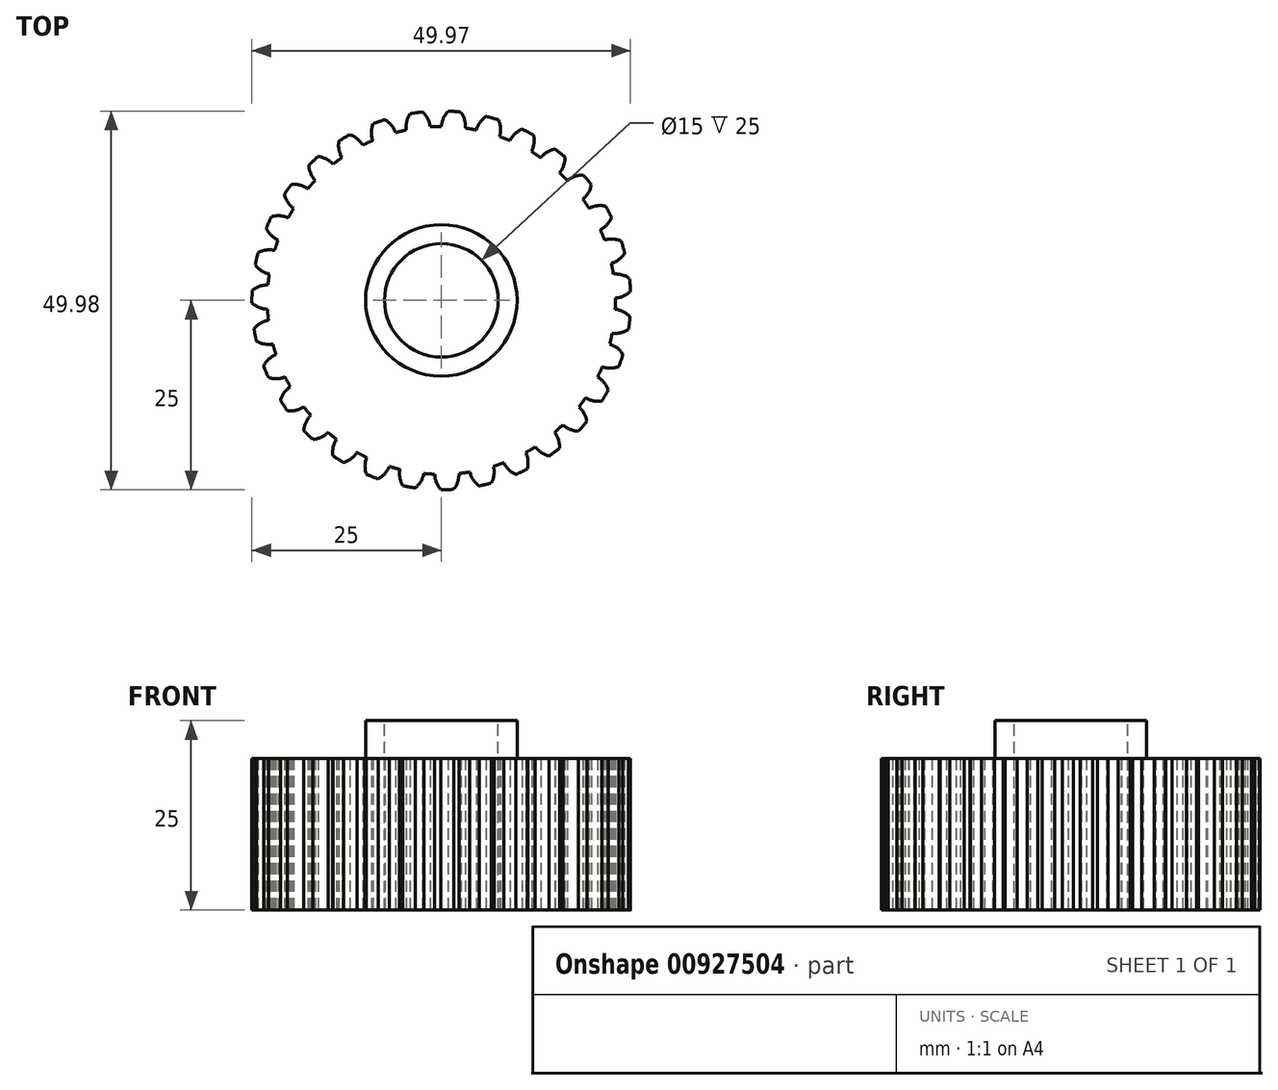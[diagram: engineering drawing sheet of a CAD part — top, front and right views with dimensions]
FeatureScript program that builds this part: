
annotation { "Feature Type Name" : "Feature", "Feature Type Description" : "" }
export const myFeature = defineFeature(function(context is Context, id is Id, definition is map)
    precondition{}
    {
        {
            var Q0;
            Q0=qCreatedBy(makeId("Top.planeOp"),FACE);
            var sketch = newSketch(context, id + "F0", { "sketchPlane" : qUnion([Q0])});
            skArc(sketch, "E0", {"start": v(2.57, 24.87) * mm, "mid": v(1.74, 24.94) * mm, "end": v(0.9, 24.98) * mm});
            skArc(sketch, "E1", {"start": v(0, 22.97) * mm, "mid": v(-0.73, 22.96) * mm, "end": v(-1.46, 22.92) * mm});
            skArc(sketch, "E2", {"start": v(3.19, 22.75) * mm, "mid": v(3.07, 23.86) * mm, "end": v(2.57, 24.87) * mm});
            skArc(sketch, "E3", {"start": v(0.9, 24.98) * mm, "mid": v(0.27, 24.06) * mm, "end": v(0, 22.97) * mm});
            skArc(sketch, "E4.1.0", {"start": v(-1.46, 22.92) * mm, "mid": v(-1.8, 24) * mm, "end": v(-2.49, 24.88) * mm});
            skArc(sketch, "E4.1.1", {"start": v(-2.49, 24.88) * mm, "mid": v(-3.32, 24.78) * mm, "end": v(-4.14, 24.65) * mm});
            skArc(sketch, "E4.1.2", {"start": v(-4.14, 24.65) * mm, "mid": v(-4.58, 23.62) * mm, "end": v(-4.62, 22.5) * mm});
            skArc(sketch, "E4.2.0", {"start": v(-6.04, 22.16) * mm, "mid": v(-6.59, 23.14) * mm, "end": v(-7.44, 23.87) * mm});
            skArc(sketch, "E4.2.1", {"start": v(-7.44, 23.87) * mm, "mid": v(-8.24, 23.6) * mm, "end": v(-9.02, 23.32) * mm});
            skArc(sketch, "E4.2.2", {"start": v(-9.02, 23.32) * mm, "mid": v(-9.24, 22.22) * mm, "end": v(-9.06, 21.1) * mm});
            skArc(sketch, "E4.3.0", {"start": v(-10.38, 20.5) * mm, "mid": v(-11.11, 21.34) * mm, "end": v(-12.1, 21.88) * mm});
            skArc(sketch, "E4.3.1", {"start": v(-12.1, 21.88) * mm, "mid": v(-12.82, 21.46) * mm, "end": v(-13.53, 21.02) * mm});
            skArc(sketch, "E4.3.2", {"start": v(-13.53, 21.02) * mm, "mid": v(-13.52, 19.9) * mm, "end": v(-13.12, 18.85) * mm});
            skArc(sketch, "E4.4.0", {"start": v(-14.29, 17.98) * mm, "mid": v(-15.18, 18.67) * mm, "end": v(-16.25, 19) * mm});
            skArc(sketch, "E4.4.1", {"start": v(-16.25, 19) * mm, "mid": v(-16.88, 18.44) * mm, "end": v(-17.48, 17.87) * mm});
            skArc(sketch, "E4.4.2", {"start": v(-17.48, 17.87) * mm, "mid": v(-17.25, 16.77) * mm, "end": v(-16.65, 15.83) * mm});
            skArc(sketch, "E4.5.0", {"start": v(-17.62, 14.74) * mm, "mid": v(-18.63, 15.23) * mm, "end": v(-19.74, 15.34) * mm});
            skArc(sketch, "E4.5.1", {"start": v(-19.74, 15.34) * mm, "mid": v(-20.24, 14.67) * mm, "end": v(-20.72, 13.98) * mm});
            skArc(sketch, "E4.5.2", {"start": v(-20.72, 13.98) * mm, "mid": v(-20.27, 12.96) * mm, "end": v(-19.5, 12.15) * mm});
            skArc(sketch, "E4.6.0", {"start": v(-20.22, 10.9) * mm, "mid": v(-21.31, 11.17) * mm, "end": v(-22.43, 11.05) * mm});
            skArc(sketch, "E4.6.1", {"start": v(-22.43, 11.05) * mm, "mid": v(-22.78, 10.3) * mm, "end": v(-23.11, 9.53) * mm});
            skArc(sketch, "E4.6.2", {"start": v(-23.11, 9.53) * mm, "mid": v(-22.46, 8.61) * mm, "end": v(-21.54, 7.98) * mm});
            skArc(sketch, "E4.7.0", {"start": v(-22, 6.6) * mm, "mid": v(-23.12, 6.65) * mm, "end": v(-24.2, 6.3) * mm});
            skArc(sketch, "E4.7.1", {"start": v(-24.2, 6.3) * mm, "mid": v(-24.39, 5.5) * mm, "end": v(-24.56, 4.68) * mm});
            skArc(sketch, "E4.7.2", {"start": v(-24.56, 4.68) * mm, "mid": v(-23.74, 3.91) * mm, "end": v(-22.7, 3.48) * mm});
            skArc(sketch, "E4.8.0", {"start": v(-22.88, 2.03) * mm, "mid": v(-23.99, 1.86) * mm, "end": v(-24.97, 1.3) * mm});
            skArc(sketch, "E4.8.1", {"start": v(-24.97, 1.3) * mm, "mid": v(-25, 0.47) * mm, "end": v(-25, -0.36) * mm});
            skArc(sketch, "E4.8.2", {"start": v(-25, -0.36) * mm, "mid": v(-24.04, -0.95) * mm, "end": v(-22.94, -1.16) * mm});
            skArc(sketch, "E4.9.0", {"start": v(-22.82, -2.61) * mm, "mid": v(-23.87, -3) * mm, "end": v(-24.72, -3.74) * mm});
            skArc(sketch, "E4.9.1", {"start": v(-24.72, -3.74) * mm, "mid": v(-24.58, -4.57) * mm, "end": v(-24.41, -5.39) * mm});
            skArc(sketch, "E4.9.2", {"start": v(-24.41, -5.39) * mm, "mid": v(-23.36, -5.77) * mm, "end": v(-22.24, -5.76) * mm});
            skArc(sketch, "E4.10.0", {"start": v(-21.83, -7.15) * mm, "mid": v(-22.78, -7.75) * mm, "end": v(-23.46, -8.64) * mm});
            skArc(sketch, "E4.10.1", {"start": v(-23.46, -8.64) * mm, "mid": v(-23.16, -9.42) * mm, "end": v(-22.83, -10.2) * mm});
            skArc(sketch, "E4.10.2", {"start": v(-22.83, -10.2) * mm, "mid": v(-21.72, -10.35) * mm, "end": v(-20.62, -10.12) * mm});
            skArc(sketch, "E4.11.0", {"start": v(-19.94, -11.4) * mm, "mid": v(-20.75, -12.18) * mm, "end": v(-21.24, -13.19) * mm});
            skArc(sketch, "E4.11.1", {"start": v(-21.24, -13.19) * mm, "mid": v(-20.79, -13.89) * mm, "end": v(-20.31, -14.58) * mm});
            skArc(sketch, "E4.11.2", {"start": v(-20.31, -14.58) * mm, "mid": v(-19.2, -14.5) * mm, "end": v(-18.16, -14.06) * mm});
            skArc(sketch, "E4.12.0", {"start": v(-17.24, -15.18) * mm, "mid": v(-17.87, -16.1) * mm, "end": v(-18.15, -17.2) * mm});
            skArc(sketch, "E4.12.1", {"start": v(-18.15, -17.2) * mm, "mid": v(-17.56, -17.79) * mm, "end": v(-16.96, -18.37) * mm});
            skArc(sketch, "E4.12.2", {"start": v(-16.96, -18.37) * mm, "mid": v(-15.88, -18.08) * mm, "end": v(-14.96, -17.43) * mm});
            skArc(sketch, "E4.13.0", {"start": v(-13.83, -18.34) * mm, "mid": v(-14.26, -19.37) * mm, "end": v(-14.32, -20.5) * mm});
            skArc(sketch, "E4.13.1", {"start": v(-14.32, -20.5) * mm, "mid": v(-13.62, -20.96) * mm, "end": v(-12.92, -21.4) * mm});
            skArc(sketch, "E4.13.2", {"start": v(-12.92, -21.4) * mm, "mid": v(-11.91, -20.9) * mm, "end": v(-11.15, -20.08) * mm});
            skArc(sketch, "E4.14.0", {"start": v(-9.85, -20.75) * mm, "mid": v(-10.07, -21.85) * mm, "end": v(-9.9, -22.96) * mm});
            skArc(sketch, "E4.14.1", {"start": v(-9.9, -22.96) * mm, "mid": v(-9.13, -23.27) * mm, "end": v(-8.34, -23.57) * mm});
            skArc(sketch, "E4.14.2", {"start": v(-8.34, -23.57) * mm, "mid": v(-7.46, -22.87) * mm, "end": v(-6.88, -21.92) * mm});
            skArc(sketch, "E4.15.0", {"start": v(-5.47, -22.3) * mm, "mid": v(-5.47, -23.43) * mm, "end": v(-5.08, -24.48) * mm});
            skArc(sketch, "E4.15.1", {"start": v(-5.08, -24.48) * mm, "mid": v(-4.25, -24.64) * mm, "end": v(-3.43, -24.76) * mm});
            skArc(sketch, "E4.15.2", {"start": v(-3.43, -24.76) * mm, "mid": v(-2.7, -23.9) * mm, "end": v(-2.32, -22.85) * mm});
            skArc(sketch, "E4.16.0", {"start": v(-0.87, -22.95) * mm, "mid": v(-0.64, -24.05) * mm, "end": v(-0.04, -25) * mm});
            skArc(sketch, "E4.16.1", {"start": v(-0.04, -25) * mm, "mid": v(0.8, -24.99) * mm, "end": v(1.63, -24.95) * mm});
            skArc(sketch, "E4.16.2", {"start": v(1.63, -24.95) * mm, "mid": v(2.16, -23.96) * mm, "end": v(2.32, -22.85) * mm});
            skArc(sketch, "E4.17.0", {"start": v(3.77, -22.66) * mm, "mid": v(4.21, -23.69) * mm, "end": v(4.99, -24.5) * mm});
            skArc(sketch, "E4.17.1", {"start": v(4.99, -24.5) * mm, "mid": v(5.8, -24.32) * mm, "end": v(6.62, -24.1) * mm});
            skArc(sketch, "E4.17.2", {"start": v(6.62, -24.1) * mm, "mid": v(6.94, -23.04) * mm, "end": v(6.88, -21.92) * mm});
            skArc(sketch, "E4.18.0", {"start": v(8.25, -21.44) * mm, "mid": v(8.9, -22.35) * mm, "end": v(9.82, -23) * mm});
            skArc(sketch, "E4.18.1", {"start": v(9.82, -23) * mm, "mid": v(10.58, -22.65) * mm, "end": v(11.33, -22.28) * mm});
            skArc(sketch, "E4.18.2", {"start": v(11.33, -22.28) * mm, "mid": v(11.44, -21.17) * mm, "end": v(11.15, -20.08) * mm});
            skArc(sketch, "E4.19.0", {"start": v(12.4, -19.34) * mm, "mid": v(13.21, -20.1) * mm, "end": v(14.25, -20.54) * mm});
            skArc(sketch, "E4.19.1", {"start": v(14.25, -20.54) * mm, "mid": v(14.92, -20.06) * mm, "end": v(15.59, -19.55) * mm});
            skArc(sketch, "E4.19.2", {"start": v(15.59, -19.55) * mm, "mid": v(15.46, -18.43) * mm, "end": v(14.96, -17.43) * mm});
            skArc(sketch, "E4.20.0", {"start": v(16.04, -16.45) * mm, "mid": v(17, -17.03) * mm, "end": v(18.09, -17.26) * mm});
            skArc(sketch, "E4.20.1", {"start": v(18.09, -17.26) * mm, "mid": v(18.66, -16.64) * mm, "end": v(19.2, -16) * mm});
            skArc(sketch, "E4.20.2", {"start": v(19.2, -16) * mm, "mid": v(18.86, -14.94) * mm, "end": v(18.16, -14.06) * mm});
            skArc(sketch, "E4.21.0", {"start": v(19.02, -12.88) * mm, "mid": v(20.07, -13.26) * mm, "end": v(21.2, -13.26) * mm});
            skArc(sketch, "E4.21.1", {"start": v(21.2, -13.26) * mm, "mid": v(21.62, -12.55) * mm, "end": v(22.03, -11.81) * mm});
            skArc(sketch, "E4.21.2", {"start": v(22.03, -11.81) * mm, "mid": v(21.48, -10.84) * mm, "end": v(20.62, -10.12) * mm});
            skArc(sketch, "E4.22.0", {"start": v(21.22, -8.79) * mm, "mid": v(22.33, -8.95) * mm, "end": v(23.43, -8.72) * mm});
            skArc(sketch, "E4.22.1", {"start": v(23.43, -8.72) * mm, "mid": v(23.7, -7.94) * mm, "end": v(23.96, -7.14) * mm});
            skArc(sketch, "E4.22.2", {"start": v(23.96, -7.14) * mm, "mid": v(23.22, -6.3) * mm, "end": v(22.24, -5.76) * mm});
            skArc(sketch, "E4.23.0", {"start": v(22.56, -4.34) * mm, "mid": v(23.68, -4.27) * mm, "end": v(24.7, -3.83) * mm});
            skArc(sketch, "E4.23.1", {"start": v(24.7, -3.83) * mm, "mid": v(24.82, -3) * mm, "end": v(24.9, -2.17) * mm});
            skArc(sketch, "E4.23.2", {"start": v(24.9, -2.17) * mm, "mid": v(24.01, -1.5) * mm, "end": v(22.94, -1.16) * mm});
            skArc(sketch, "E4.24.0", {"start": v(22.97, 0.3) * mm, "mid": v(24.05, 0.58) * mm, "end": v(24.97, 1.22) * mm});
            skArc(sketch, "E4.24.1", {"start": v(24.97, 1.22) * mm, "mid": v(24.92, 2.06) * mm, "end": v(24.83, 2.89) * mm});
            skArc(sketch, "E4.24.2", {"start": v(24.83, 2.89) * mm, "mid": v(23.82, 3.37) * mm, "end": v(22.7, 3.48) * mm});
            skArc(sketch, "E4.25.0", {"start": v(22.44, 4.9) * mm, "mid": v(23.44, 5.4) * mm, "end": v(24.21, 6.22) * mm});
            skArc(sketch, "E4.25.1", {"start": v(24.21, 6.22) * mm, "mid": v(24, 7.03) * mm, "end": v(23.74, 7.83) * mm});
            skArc(sketch, "E4.25.2", {"start": v(23.74, 7.83) * mm, "mid": v(22.65, 8.1) * mm, "end": v(21.54, 7.98) * mm});
            skArc(sketch, "E4.26.0", {"start": v(21, 9.33) * mm, "mid": v(21.87, 10.02) * mm, "end": v(22.46, 10.97) * mm});
            skArc(sketch, "E4.26.1", {"start": v(22.46, 10.97) * mm, "mid": v(22.08, 11.72) * mm, "end": v(21.68, 12.45) * mm});
            skArc(sketch, "E4.26.2", {"start": v(21.68, 12.45) * mm, "mid": v(20.56, 12.5) * mm, "end": v(19.5, 12.15) * mm});
            skArc(sketch, "E4.27.0", {"start": v(18.68, 13.36) * mm, "mid": v(19.41, 14.22) * mm, "end": v(19.8, 15.27) * mm});
            skArc(sketch, "E4.27.1", {"start": v(19.8, 15.27) * mm, "mid": v(19.27, 15.92) * mm, "end": v(18.73, 16.56) * mm});
            skArc(sketch, "E4.27.2", {"start": v(18.73, 16.56) * mm, "mid": v(17.62, 16.38) * mm, "end": v(16.65, 15.83) * mm});
            skArc(sketch, "E4.28.0", {"start": v(15.61, 16.85) * mm, "mid": v(16.15, 17.83) * mm, "end": v(16.32, 18.94) * mm});
            skArc(sketch, "E4.28.1", {"start": v(16.32, 18.94) * mm, "mid": v(15.67, 19.48) * mm, "end": v(15.01, 19.99) * mm});
            skArc(sketch, "E4.28.2", {"start": v(15.01, 19.99) * mm, "mid": v(13.97, 19.59) * mm, "end": v(13.12, 18.85) * mm});
            skArc(sketch, "E4.29.0", {"start": v(11.9, 19.65) * mm, "mid": v(12.23, 20.72) * mm, "end": v(12.17, 21.84) * mm});
            skArc(sketch, "E4.29.1", {"start": v(12.17, 21.84) * mm, "mid": v(11.43, 22.23) * mm, "end": v(10.68, 22.6) * mm});
            skArc(sketch, "E4.29.2", {"start": v(10.68, 22.6) * mm, "mid": v(9.74, 22) * mm, "end": v(9.06, 21.1) * mm});
            skArc(sketch, "E4.30.0", {"start": v(7.7, 21.64) * mm, "mid": v(7.81, 22.76) * mm, "end": v(7.53, 23.84) * mm});
            skArc(sketch, "E4.30.1", {"start": v(7.53, 23.84) * mm, "mid": v(6.72, 24.08) * mm, "end": v(5.92, 24.3) * mm});
            skArc(sketch, "E4.30.2", {"start": v(5.92, 24.3) * mm, "mid": v(5.11, 23.5) * mm, "end": v(4.62, 22.5) * mm});
            skArc(sketch, "E5.trimOffspring", {"start": v(-4.62, 22.5) * mm, "mid": v(-5.33, 22.34) * mm, "end": v(-6.04, 22.16) * mm});
            skArc(sketch, "E6.trimOffspring", {"start": v(-9.06, 21.1) * mm, "mid": v(-9.72, 20.81) * mm, "end": v(-10.38, 20.5) * mm});
            skArc(sketch, "E7.trimOffspring", {"start": v(-13.12, 18.85) * mm, "mid": v(5.33, -22.34) * mm, "end": v(3.19, 22.75) * mm});
            skSolve(sketch);
        }
        {
            var Q0;
            Q0=makeQuery(id+"F0.imprint","IMPRINT",FACE,{"disambiguationData":[TD([[makeQuery(id+"F0.imprint","IMPRINT",EDGE,{"derivedFrom":sQuery(id+"F0.wireOp",EDGE,"E0")}),1.0]])]});
            var Q1;
            {var subQ0=sQuery(id+"F0.wireOp",EDGE,"E4.4.0");Q1=makeQuery(id+"F0.imprint","IMPRINT",FACE,{"disambiguationData":[TD([[makeQuery(id+"F0.imprint","IMPRINT",EDGE,{"derivedFrom":subQ0}),1.0]])]});}
            var Q2;
            {var subQ0=sQuery(id+"F0.wireOp",EDGE,"E4.5.0");Q2=makeQuery(id+"F0.imprint","IMPRINT",FACE,{"disambiguationData":[TD([[makeQuery(id+"F0.imprint","IMPRINT",EDGE,{"derivedFrom":subQ0}),1.0]])]});}
            var Q3;
            {var subQ0=sQuery(id+"F0.wireOp",EDGE,"E4.6.0");Q3=makeQuery(id+"F0.imprint","IMPRINT",FACE,{"disambiguationData":[TD([[makeQuery(id+"F0.imprint","IMPRINT",EDGE,{"derivedFrom":subQ0}),1.0]])]});}
            var Q4;
            {var subQ0=sQuery(id+"F0.wireOp",EDGE,"E4.7.0");Q4=makeQuery(id+"F0.imprint","IMPRINT",FACE,{"disambiguationData":[TD([[makeQuery(id+"F0.imprint","IMPRINT",EDGE,{"derivedFrom":subQ0}),1.0]])]});}
            var Q5;
            {var subQ0=sQuery(id+"F0.wireOp",EDGE,"E4.8.0");Q5=makeQuery(id+"F0.imprint","IMPRINT",FACE,{"disambiguationData":[TD([[makeQuery(id+"F0.imprint","IMPRINT",EDGE,{"derivedFrom":subQ0}),1.0]])]});}
            var Q6;
            {var subQ0=sQuery(id+"F0.wireOp",EDGE,"E4.9.0");Q6=makeQuery(id+"F0.imprint","IMPRINT",FACE,{"disambiguationData":[TD([[makeQuery(id+"F0.imprint","IMPRINT",EDGE,{"derivedFrom":subQ0}),1.0]])]});}
            var Q7;
            {var subQ0=sQuery(id+"F0.wireOp",EDGE,"E4.10.0");Q7=makeQuery(id+"F0.imprint","IMPRINT",FACE,{"disambiguationData":[TD([[makeQuery(id+"F0.imprint","IMPRINT",EDGE,{"derivedFrom":subQ0}),1.0]])]});}
            var Q8;
            {var subQ0=sQuery(id+"F0.wireOp",EDGE,"E4.11.0");Q8=makeQuery(id+"F0.imprint","IMPRINT",FACE,{"disambiguationData":[TD([[makeQuery(id+"F0.imprint","IMPRINT",EDGE,{"derivedFrom":subQ0}),1.0]])]});}
            var Q9;
            {var subQ0=sQuery(id+"F0.wireOp",EDGE,"E4.12.0");Q9=makeQuery(id+"F0.imprint","IMPRINT",FACE,{"disambiguationData":[TD([[makeQuery(id+"F0.imprint","IMPRINT",EDGE,{"derivedFrom":subQ0}),1.0]])]});}
            var Q10;
            {var subQ0=sQuery(id+"F0.wireOp",EDGE,"E4.13.0");Q10=makeQuery(id+"F0.imprint","IMPRINT",FACE,{"disambiguationData":[TD([[makeQuery(id+"F0.imprint","IMPRINT",EDGE,{"derivedFrom":subQ0}),1.0]])]});}
            var Q11;
            {var subQ0=sQuery(id+"F0.wireOp",EDGE,"E4.14.0");Q11=makeQuery(id+"F0.imprint","IMPRINT",FACE,{"disambiguationData":[TD([[makeQuery(id+"F0.imprint","IMPRINT",EDGE,{"derivedFrom":subQ0}),1.0]])]});}
            var Q12;
            {var subQ0=sQuery(id+"F0.wireOp",EDGE,"E4.15.0");Q12=makeQuery(id+"F0.imprint","IMPRINT",FACE,{"disambiguationData":[TD([[makeQuery(id+"F0.imprint","IMPRINT",EDGE,{"derivedFrom":subQ0}),1.0]])]});}
            var Q13;
            {var subQ0=sQuery(id+"F0.wireOp",EDGE,"E4.16.0");Q13=makeQuery(id+"F0.imprint","IMPRINT",FACE,{"disambiguationData":[TD([[makeQuery(id+"F0.imprint","IMPRINT",EDGE,{"derivedFrom":subQ0}),1.0]])]});}
            var Q14;
            {var subQ0=sQuery(id+"F0.wireOp",EDGE,"E4.17.0");Q14=makeQuery(id+"F0.imprint","IMPRINT",FACE,{"disambiguationData":[TD([[makeQuery(id+"F0.imprint","IMPRINT",EDGE,{"derivedFrom":subQ0}),1.0]])]});}
            var Q15;
            {var subQ0=sQuery(id+"F0.wireOp",EDGE,"E4.18.0");Q15=makeQuery(id+"F0.imprint","IMPRINT",FACE,{"disambiguationData":[TD([[makeQuery(id+"F0.imprint","IMPRINT",EDGE,{"derivedFrom":subQ0}),1.0]])]});}
            var Q16;
            {var subQ0=sQuery(id+"F0.wireOp",EDGE,"E4.19.0");Q16=makeQuery(id+"F0.imprint","IMPRINT",FACE,{"disambiguationData":[TD([[makeQuery(id+"F0.imprint","IMPRINT",EDGE,{"derivedFrom":subQ0}),1.0]])]});}
            var Q17;
            {var subQ0=sQuery(id+"F0.wireOp",EDGE,"E4.20.0");Q17=makeQuery(id+"F0.imprint","IMPRINT",FACE,{"disambiguationData":[TD([[makeQuery(id+"F0.imprint","IMPRINT",EDGE,{"derivedFrom":subQ0}),1.0]])]});}
            var Q18;
            {var subQ0=sQuery(id+"F0.wireOp",EDGE,"E4.21.0");Q18=makeQuery(id+"F0.imprint","IMPRINT",FACE,{"disambiguationData":[TD([[makeQuery(id+"F0.imprint","IMPRINT",EDGE,{"derivedFrom":subQ0}),1.0]])]});}
            var Q19;
            {var subQ0=sQuery(id+"F0.wireOp",EDGE,"E4.22.0");Q19=makeQuery(id+"F0.imprint","IMPRINT",FACE,{"disambiguationData":[TD([[makeQuery(id+"F0.imprint","IMPRINT",EDGE,{"derivedFrom":subQ0}),1.0]])]});}
            var Q20;
            {var subQ0=sQuery(id+"F0.wireOp",EDGE,"E4.23.0");Q20=makeQuery(id+"F0.imprint","IMPRINT",FACE,{"disambiguationData":[TD([[makeQuery(id+"F0.imprint","IMPRINT",EDGE,{"derivedFrom":subQ0}),1.0]])]});}
            var Q21;
            {var subQ0=sQuery(id+"F0.wireOp",EDGE,"E4.24.0");Q21=makeQuery(id+"F0.imprint","IMPRINT",FACE,{"disambiguationData":[TD([[makeQuery(id+"F0.imprint","IMPRINT",EDGE,{"derivedFrom":subQ0}),1.0]])]});}
            var Q22;
            {var subQ0=sQuery(id+"F0.wireOp",EDGE,"E4.25.0");Q22=makeQuery(id+"F0.imprint","IMPRINT",FACE,{"disambiguationData":[TD([[makeQuery(id+"F0.imprint","IMPRINT",EDGE,{"derivedFrom":subQ0}),1.0]])]});}
            var Q23;
            {var subQ0=sQuery(id+"F0.wireOp",EDGE,"E4.26.0");Q23=makeQuery(id+"F0.imprint","IMPRINT",FACE,{"disambiguationData":[TD([[makeQuery(id+"F0.imprint","IMPRINT",EDGE,{"derivedFrom":subQ0}),1.0]])]});}
            var Q24;
            {var subQ0=sQuery(id+"F0.wireOp",EDGE,"E4.27.0");Q24=makeQuery(id+"F0.imprint","IMPRINT",FACE,{"disambiguationData":[TD([[makeQuery(id+"F0.imprint","IMPRINT",EDGE,{"derivedFrom":subQ0}),1.0]])]});}
            var Q25;
            {var subQ0=sQuery(id+"F0.wireOp",EDGE,"E4.28.0");Q25=makeQuery(id+"F0.imprint","IMPRINT",FACE,{"disambiguationData":[TD([[makeQuery(id+"F0.imprint","IMPRINT",EDGE,{"derivedFrom":subQ0}),1.0]])]});}
            var Q26;
            {var subQ0=sQuery(id+"F0.wireOp",EDGE,"E4.29.0");Q26=makeQuery(id+"F0.imprint","IMPRINT",FACE,{"disambiguationData":[TD([[makeQuery(id+"F0.imprint","IMPRINT",EDGE,{"derivedFrom":subQ0}),1.0]])]});}
            var Q27;
            {var subQ0=sQuery(id+"F0.wireOp",EDGE,"E4.30.0");Q27=makeQuery(id+"F0.imprint","IMPRINT",FACE,{"disambiguationData":[TD([[makeQuery(id+"F0.imprint","IMPRINT",EDGE,{"derivedFrom":subQ0}),1.0]])]});}
            extrude(context, id + "F1", {"entities" : qUnion([Q0, Q1, Q2, Q3, Q4, Q5, Q6, Q7, Q8, Q9, Q10, Q11, Q12, Q13, Q14, Q15, Q16, Q17, Q18, Q19, Q20, Q21, Q22, Q23, Q24, Q25, Q26, Q27]), "depth" : 20 * mm, "offsetDistance" : 25 * mm});
        }
        {
            var Q0;
            Q0=makeQuery(id+"F1.opExtrude","CAP_FACE",FACE,{"disambiguationData":[OSD([sQuery(id+"F0.wireOp",EDGE,"E0"),sQuery(id+"F0.wireOp",EDGE,"E1"),sQuery(id+"F0.wireOp",EDGE,"E2"),sQuery(id+"F0.wireOp",EDGE,"E3"),sQuery(id+"F0.wireOp",EDGE,"E4.1.0"),sQuery(id+"F0.wireOp",EDGE,"E4.1.1"),sQuery(id+"F0.wireOp",EDGE,"E4.1.2"),sQuery(id+"F0.wireOp",EDGE,"E4.2.0"),sQuery(id+"F0.wireOp",EDGE,"E4.2.1"),sQuery(id+"F0.wireOp",EDGE,"E4.2.2"),sQuery(id+"F0.wireOp",EDGE,"E4.3.0"),sQuery(id+"F0.wireOp",EDGE,"E4.3.1"),sQuery(id+"F0.wireOp",EDGE,"E4.3.2"),sQuery(id+"F0.wireOp",EDGE,"E4.4.0"),sQuery(id+"F0.wireOp",EDGE,"E4.4.1"),sQuery(id+"F0.wireOp",EDGE,"E4.4.2"),sQuery(id+"F0.wireOp",EDGE,"E4.5.0"),sQuery(id+"F0.wireOp",EDGE,"E4.5.1"),sQuery(id+"F0.wireOp",EDGE,"E4.5.2"),sQuery(id+"F0.wireOp",EDGE,"E4.6.0"),sQuery(id+"F0.wireOp",EDGE,"E4.6.1"),sQuery(id+"F0.wireOp",EDGE,"E4.6.2"),sQuery(id+"F0.wireOp",EDGE,"E4.7.0"),sQuery(id+"F0.wireOp",EDGE,"E4.7.1"),sQuery(id+"F0.wireOp",EDGE,"E4.7.2"),sQuery(id+"F0.wireOp",EDGE,"E4.8.0"),sQuery(id+"F0.wireOp",EDGE,"E4.8.1"),sQuery(id+"F0.wireOp",EDGE,"E4.8.2"),sQuery(id+"F0.wireOp",EDGE,"E4.9.0"),sQuery(id+"F0.wireOp",EDGE,"E4.9.1"),sQuery(id+"F0.wireOp",EDGE,"E4.9.2"),sQuery(id+"F0.wireOp",EDGE,"E4.10.0"),sQuery(id+"F0.wireOp",EDGE,"E4.10.1"),sQuery(id+"F0.wireOp",EDGE,"E4.10.2"),sQuery(id+"F0.wireOp",EDGE,"E4.11.0"),sQuery(id+"F0.wireOp",EDGE,"E4.11.1"),sQuery(id+"F0.wireOp",EDGE,"E4.11.2"),sQuery(id+"F0.wireOp",EDGE,"E4.12.0"),sQuery(id+"F0.wireOp",EDGE,"E4.12.1"),sQuery(id+"F0.wireOp",EDGE,"E4.12.2"),sQuery(id+"F0.wireOp",EDGE,"E4.13.0"),sQuery(id+"F0.wireOp",EDGE,"E4.13.1"),sQuery(id+"F0.wireOp",EDGE,"E4.13.2"),sQuery(id+"F0.wireOp",EDGE,"E4.14.0"),sQuery(id+"F0.wireOp",EDGE,"E4.14.1"),sQuery(id+"F0.wireOp",EDGE,"E4.14.2"),sQuery(id+"F0.wireOp",EDGE,"E4.15.0"),sQuery(id+"F0.wireOp",EDGE,"E4.15.1"),sQuery(id+"F0.wireOp",EDGE,"E4.15.2"),sQuery(id+"F0.wireOp",EDGE,"E4.16.0"),sQuery(id+"F0.wireOp",EDGE,"E4.16.1"),sQuery(id+"F0.wireOp",EDGE,"E4.16.2"),sQuery(id+"F0.wireOp",EDGE,"E4.17.0"),sQuery(id+"F0.wireOp",EDGE,"E4.17.1"),sQuery(id+"F0.wireOp",EDGE,"E4.17.2"),sQuery(id+"F0.wireOp",EDGE,"E4.18.0"),sQuery(id+"F0.wireOp",EDGE,"E4.18.1"),sQuery(id+"F0.wireOp",EDGE,"E4.18.2"),sQuery(id+"F0.wireOp",EDGE,"E4.19.0"),sQuery(id+"F0.wireOp",EDGE,"E4.19.1"),sQuery(id+"F0.wireOp",EDGE,"E4.19.2"),sQuery(id+"F0.wireOp",EDGE,"E4.20.0"),sQuery(id+"F0.wireOp",EDGE,"E4.20.1"),sQuery(id+"F0.wireOp",EDGE,"E4.20.2"),sQuery(id+"F0.wireOp",EDGE,"E4.21.0"),sQuery(id+"F0.wireOp",EDGE,"E4.21.1"),sQuery(id+"F0.wireOp",EDGE,"E4.21.2"),sQuery(id+"F0.wireOp",EDGE,"E4.22.0"),sQuery(id+"F0.wireOp",EDGE,"E4.22.1"),sQuery(id+"F0.wireOp",EDGE,"E4.22.2"),sQuery(id+"F0.wireOp",EDGE,"E4.23.0"),sQuery(id+"F0.wireOp",EDGE,"E4.23.1"),sQuery(id+"F0.wireOp",EDGE,"E4.23.2"),sQuery(id+"F0.wireOp",EDGE,"E4.24.0"),sQuery(id+"F0.wireOp",EDGE,"E4.24.1"),sQuery(id+"F0.wireOp",EDGE,"E4.24.2"),sQuery(id+"F0.wireOp",EDGE,"E4.25.0"),sQuery(id+"F0.wireOp",EDGE,"E4.25.1"),sQuery(id+"F0.wireOp",EDGE,"E4.25.2"),sQuery(id+"F0.wireOp",EDGE,"E4.26.0"),sQuery(id+"F0.wireOp",EDGE,"E4.26.1"),sQuery(id+"F0.wireOp",EDGE,"E4.26.2"),sQuery(id+"F0.wireOp",EDGE,"E4.27.0"),sQuery(id+"F0.wireOp",EDGE,"E4.27.1"),sQuery(id+"F0.wireOp",EDGE,"E4.27.2"),sQuery(id+"F0.wireOp",EDGE,"E4.28.0"),sQuery(id+"F0.wireOp",EDGE,"E4.28.1"),sQuery(id+"F0.wireOp",EDGE,"E4.28.2"),sQuery(id+"F0.wireOp",EDGE,"E4.29.0"),sQuery(id+"F0.wireOp",EDGE,"E4.29.1"),sQuery(id+"F0.wireOp",EDGE,"E4.29.2"),sQuery(id+"F0.wireOp",EDGE,"E4.30.0"),sQuery(id+"F0.wireOp",EDGE,"E4.30.1"),sQuery(id+"F0.wireOp",EDGE,"E4.30.2"),sQuery(id+"F0.wireOp",EDGE,"E5.trimOffspring"),sQuery(id+"F0.wireOp",EDGE,"E6.trimOffspring"),sQuery(id+"F0.wireOp",EDGE,"E7.trimOffspring")])],"isStart":false});
            var sketch = newSketch(context, id + "F2", { "sketchPlane" : qUnion([Q0])});
            skCircle(sketch, "E8", {"center": v(0, 0) * mm, "radius": 7.5 * mm});
            skSolve(sketch);
        }
        {
            var Q0;
            Q0=makeQuery(id+"F2.imprint","IMPRINT",FACE,{"disambiguationData":[TD([[makeQuery(id+"F2.imprint","IMPRINT",EDGE,{"derivedFrom":sQuery(id+"F2.wireOp",EDGE,"E8")}),1.0]])]});
            extrude(context, id + "F3", {"entities" : qUnion([Q0]), "operationType" : NewBodyOperationType.REMOVE, "oppositeDirection" : true, "depth" : 53 * mm, "offsetDistance" : 25 * mm});
        }
        {
            var Q0;
            Q0=makeQuery(id+"F1.opExtrude","CAP_FACE",FACE,{"disambiguationData":[OSD([sQuery(id+"F0.wireOp",EDGE,"E0"),sQuery(id+"F0.wireOp",EDGE,"E1"),sQuery(id+"F0.wireOp",EDGE,"E2"),sQuery(id+"F0.wireOp",EDGE,"E3"),sQuery(id+"F0.wireOp",EDGE,"E4.1.0"),sQuery(id+"F0.wireOp",EDGE,"E4.1.1"),sQuery(id+"F0.wireOp",EDGE,"E4.1.2"),sQuery(id+"F0.wireOp",EDGE,"E4.2.0"),sQuery(id+"F0.wireOp",EDGE,"E4.2.1"),sQuery(id+"F0.wireOp",EDGE,"E4.2.2"),sQuery(id+"F0.wireOp",EDGE,"E4.3.0"),sQuery(id+"F0.wireOp",EDGE,"E4.3.1"),sQuery(id+"F0.wireOp",EDGE,"E4.3.2"),sQuery(id+"F0.wireOp",EDGE,"E4.4.0"),sQuery(id+"F0.wireOp",EDGE,"E4.4.1"),sQuery(id+"F0.wireOp",EDGE,"E4.4.2"),sQuery(id+"F0.wireOp",EDGE,"E4.5.0"),sQuery(id+"F0.wireOp",EDGE,"E4.5.1"),sQuery(id+"F0.wireOp",EDGE,"E4.5.2"),sQuery(id+"F0.wireOp",EDGE,"E4.6.0"),sQuery(id+"F0.wireOp",EDGE,"E4.6.1"),sQuery(id+"F0.wireOp",EDGE,"E4.6.2"),sQuery(id+"F0.wireOp",EDGE,"E4.7.0"),sQuery(id+"F0.wireOp",EDGE,"E4.7.1"),sQuery(id+"F0.wireOp",EDGE,"E4.7.2"),sQuery(id+"F0.wireOp",EDGE,"E4.8.0"),sQuery(id+"F0.wireOp",EDGE,"E4.8.1"),sQuery(id+"F0.wireOp",EDGE,"E4.8.2"),sQuery(id+"F0.wireOp",EDGE,"E4.9.0"),sQuery(id+"F0.wireOp",EDGE,"E4.9.1"),sQuery(id+"F0.wireOp",EDGE,"E4.9.2"),sQuery(id+"F0.wireOp",EDGE,"E4.10.0"),sQuery(id+"F0.wireOp",EDGE,"E4.10.1"),sQuery(id+"F0.wireOp",EDGE,"E4.10.2"),sQuery(id+"F0.wireOp",EDGE,"E4.11.0"),sQuery(id+"F0.wireOp",EDGE,"E4.11.1"),sQuery(id+"F0.wireOp",EDGE,"E4.11.2"),sQuery(id+"F0.wireOp",EDGE,"E4.12.0"),sQuery(id+"F0.wireOp",EDGE,"E4.12.1"),sQuery(id+"F0.wireOp",EDGE,"E4.12.2"),sQuery(id+"F0.wireOp",EDGE,"E4.13.0"),sQuery(id+"F0.wireOp",EDGE,"E4.13.1"),sQuery(id+"F0.wireOp",EDGE,"E4.13.2"),sQuery(id+"F0.wireOp",EDGE,"E4.14.0"),sQuery(id+"F0.wireOp",EDGE,"E4.14.1"),sQuery(id+"F0.wireOp",EDGE,"E4.14.2"),sQuery(id+"F0.wireOp",EDGE,"E4.15.0"),sQuery(id+"F0.wireOp",EDGE,"E4.15.1"),sQuery(id+"F0.wireOp",EDGE,"E4.15.2"),sQuery(id+"F0.wireOp",EDGE,"E4.16.0"),sQuery(id+"F0.wireOp",EDGE,"E4.16.1"),sQuery(id+"F0.wireOp",EDGE,"E4.16.2"),sQuery(id+"F0.wireOp",EDGE,"E4.17.0"),sQuery(id+"F0.wireOp",EDGE,"E4.17.1"),sQuery(id+"F0.wireOp",EDGE,"E4.17.2"),sQuery(id+"F0.wireOp",EDGE,"E4.18.0"),sQuery(id+"F0.wireOp",EDGE,"E4.18.1"),sQuery(id+"F0.wireOp",EDGE,"E4.18.2"),sQuery(id+"F0.wireOp",EDGE,"E4.19.0"),sQuery(id+"F0.wireOp",EDGE,"E4.19.1"),sQuery(id+"F0.wireOp",EDGE,"E4.19.2"),sQuery(id+"F0.wireOp",EDGE,"E4.20.0"),sQuery(id+"F0.wireOp",EDGE,"E4.20.1"),sQuery(id+"F0.wireOp",EDGE,"E4.20.2"),sQuery(id+"F0.wireOp",EDGE,"E4.21.0"),sQuery(id+"F0.wireOp",EDGE,"E4.21.1"),sQuery(id+"F0.wireOp",EDGE,"E4.21.2"),sQuery(id+"F0.wireOp",EDGE,"E4.22.0"),sQuery(id+"F0.wireOp",EDGE,"E4.22.1"),sQuery(id+"F0.wireOp",EDGE,"E4.22.2"),sQuery(id+"F0.wireOp",EDGE,"E4.23.0"),sQuery(id+"F0.wireOp",EDGE,"E4.23.1"),sQuery(id+"F0.wireOp",EDGE,"E4.23.2"),sQuery(id+"F0.wireOp",EDGE,"E4.24.0"),sQuery(id+"F0.wireOp",EDGE,"E4.24.1"),sQuery(id+"F0.wireOp",EDGE,"E4.24.2"),sQuery(id+"F0.wireOp",EDGE,"E4.25.0"),sQuery(id+"F0.wireOp",EDGE,"E4.25.1"),sQuery(id+"F0.wireOp",EDGE,"E4.25.2"),sQuery(id+"F0.wireOp",EDGE,"E4.26.0"),sQuery(id+"F0.wireOp",EDGE,"E4.26.1"),sQuery(id+"F0.wireOp",EDGE,"E4.26.2"),sQuery(id+"F0.wireOp",EDGE,"E4.27.0"),sQuery(id+"F0.wireOp",EDGE,"E4.27.1"),sQuery(id+"F0.wireOp",EDGE,"E4.27.2"),sQuery(id+"F0.wireOp",EDGE,"E4.28.0"),sQuery(id+"F0.wireOp",EDGE,"E4.28.1"),sQuery(id+"F0.wireOp",EDGE,"E4.28.2"),sQuery(id+"F0.wireOp",EDGE,"E4.29.0"),sQuery(id+"F0.wireOp",EDGE,"E4.29.1"),sQuery(id+"F0.wireOp",EDGE,"E4.29.2"),sQuery(id+"F0.wireOp",EDGE,"E4.30.0"),sQuery(id+"F0.wireOp",EDGE,"E4.30.1"),sQuery(id+"F0.wireOp",EDGE,"E4.30.2"),sQuery(id+"F0.wireOp",EDGE,"E5.trimOffspring"),sQuery(id+"F0.wireOp",EDGE,"E6.trimOffspring"),sQuery(id+"F0.wireOp",EDGE,"E7.trimOffspring")])],"isStart":false});
            var sketch = newSketch(context, id + "F4", { "sketchPlane" : qUnion([Q0])});
            skCircle(sketch, "E9", {"center": v(0, 0) * mm, "radius": 7.5 * mm});
            skCircle(sketch, "E10", {"center": v(0, 0) * mm, "radius": 10 * mm});
            skSolve(sketch);
        }
        {
            var Q0;
            Q0 = qSketchRegion(id + "F4", true);
            extrude(context, id + "F5", {"entities" : qUnion([Q0]), "operationType" : NewBodyOperationType.ADD, "depth" : 5 * mm, "offsetDistance" : 25 * mm});
        }
    });
